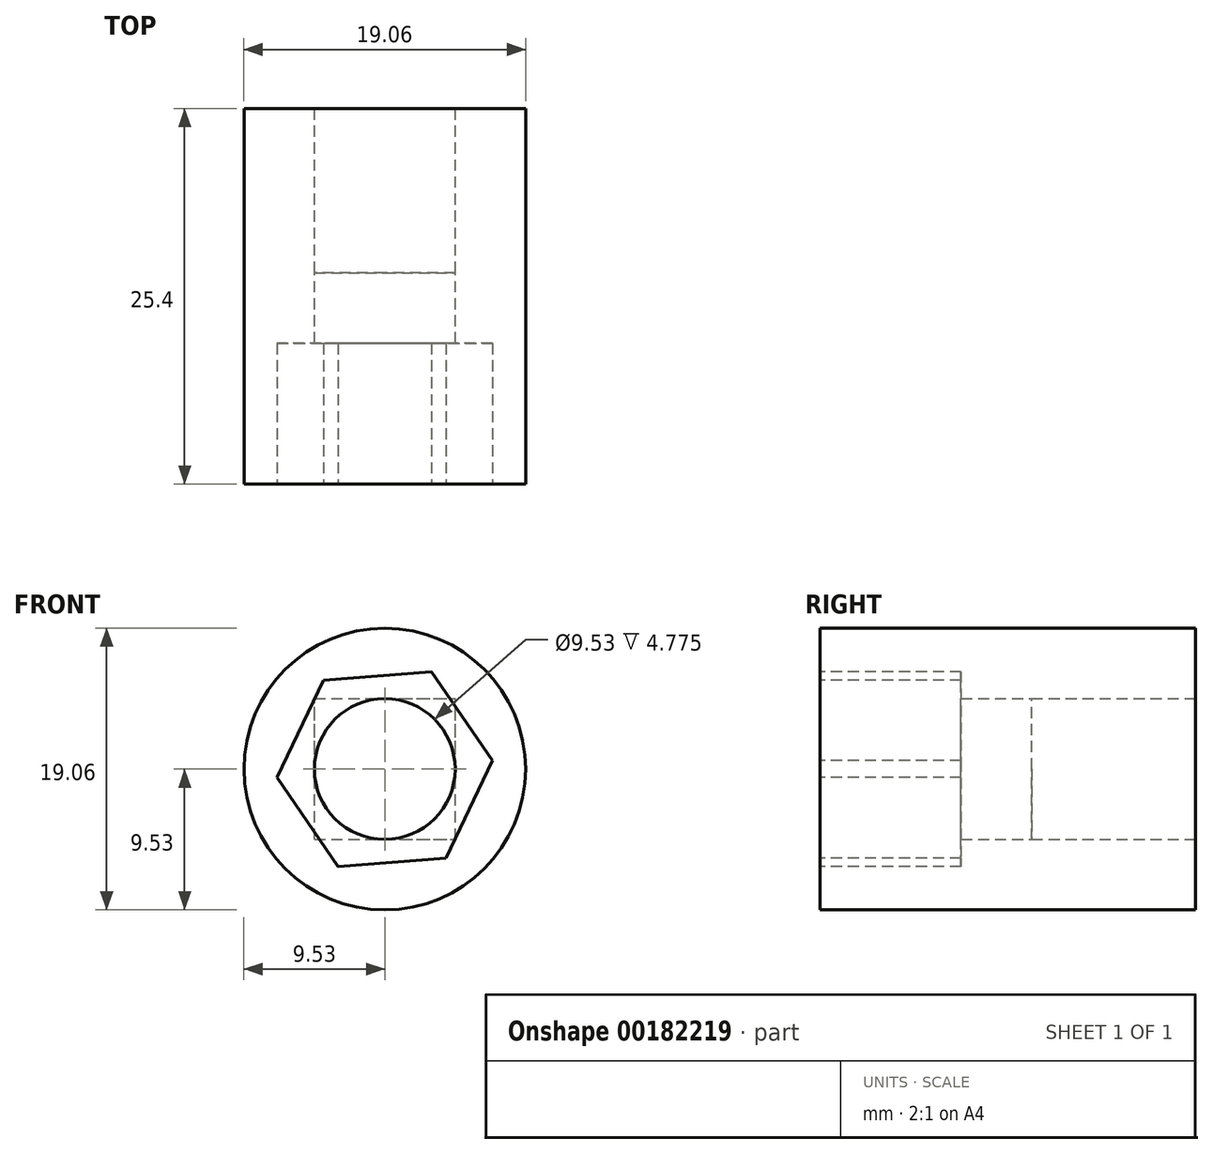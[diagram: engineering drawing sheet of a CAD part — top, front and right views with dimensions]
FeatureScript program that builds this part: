
annotation { "Feature Type Name" : "Feature", "Feature Type Description" : "" }
export const myFeature = defineFeature(function(context is Context, id is Id, definition is map)
    precondition{}
    {
        {
            var Q0;
            Q0=qCreatedBy(makeId("Front.planeOp"),FACE);
            var sketch = newSketch(context, id + "F0", { "sketchPlane" : qUnion([Q0])});
            skCircle(sketch, "E0", {"center": v(0, 0) * mm, "radius": 9.53 * mm});
            skSolve(sketch);
        }
        {
            var Q0;
            Q0 = qSketchRegion(id + "F0", true);
            extrude(context, id + "F1", {"entities" : qUnion([Q0]), "depth" : 25.4 * mm});
        }
        {
            var Q0;
            Q0=qCreatedBy(makeId("Front.planeOp"),FACE);
            var sketch = newSketch(context, id + "F2", { "sketchPlane" : qUnion([Q0])});
            skCircle(sketch, "E1", {"center": v(0, 0) * mm, "radius": 4.76 * mm});
            skLineSegment(sketch, "E2.bottom", {"start": v(-4.76, -4.76) * mm, "end": v(4.76, -4.76) * mm});
            skLineSegment(sketch, "E2.top", {"start": v(-4.76, 4.76) * mm, "end": v(4.76, 4.76) * mm});
            skLineSegment(sketch, "E2.left", {"start": v(-4.76, -4.76) * mm, "end": v(-4.76, 4.76) * mm});
            skLineSegment(sketch, "E2.right", {"start": v(4.76, -4.76) * mm, "end": v(4.76, 4.76) * mm});
            skSolve(sketch);
        }
        {
            var Q0;
            {var subQ0=sQuery(id+"F2.wireOp",EDGE,"E1");var subQ1=makeQuery(id+"F2.imprint","INTERSECT",VERTEX,{"derivedFrom":[subQ0,sQuery(id+"F2.wireOp",EDGE,"E2.top")]});Q0=makeQuery(id+"F2.imprint","IMPRINT",FACE,{"disambiguationData":[TD([[makeQuery(id+"F2.imprint","IMPRINT",EDGE,{"disambiguationData":[TD([[subQ1,1.0]])],"derivedFrom":subQ0}),1.0]])]});}
            extrude(context, id + "F3", {"entities" : qUnion([Q0]), "operationType" : NewBodyOperationType.REMOVE, "endBound" : BoundingType.THROUGH_ALL, "depth" : 25.4 * mm});
        }
        {
            var Q0;
            Q0 = qSketchRegion(id + "F2", true);
            extrude(context, id + "F4", {"entities" : qUnion([Q0]), "operationType" : NewBodyOperationType.REMOVE, "depth" : 11.1 * mm});
        }
        {
            var Q0;
            Q0=makeQuery(id+"F1.opExtrude","CAP_FACE",FACE,{"disambiguationData":[OSD([sQuery(id+"F0.wireOp",EDGE,"E0")])],"isStart":false});
            var sketch = newSketch(context, id + "F5", { "sketchPlane" : qUnion([Q0])});
            skCircle(sketch, "E3.cCircle", {"center": v(0, 0) * mm, "radius": 6.32 * mm, "construction": true});
            skLineSegment(sketch, "E3.0", {"start": v(-3.15, -6.59) * mm, "end": v(-7.28, -0.57) * mm});
            skLineSegment(sketch, "E3.1", {"start": v(-7.28, -0.57) * mm, "end": v(-4.13, 6.02) * mm});
            skLineSegment(sketch, "E3.2", {"start": v(-4.13, 6.02) * mm, "end": v(3.15, 6.59) * mm});
            skLineSegment(sketch, "E3.3", {"start": v(3.15, 6.59) * mm, "end": v(7.28, 0.57) * mm});
            skLineSegment(sketch, "E3.4", {"start": v(7.28, 0.57) * mm, "end": v(4.13, -6.02) * mm});
            skLineSegment(sketch, "E3.5", {"start": v(4.13, -6.02) * mm, "end": v(-3.15, -6.59) * mm});
            skPoint(sketch, "E3.0.midPoint", {"position": v(-5.22, -3.58) * mm});
            skSolve(sketch);
        }
        {
            var Q0;
            Q0 = qSketchRegion(id + "F5", true);
            extrude(context, id + "F6", {"entities" : qUnion([Q0]), "operationType" : NewBodyOperationType.REMOVE, "oppositeDirection" : true, "depth" : 9.52 * mm});
        }
    });
